# Revit family: Haworth_Tilt_Stool
name_source: partatom
category: Furniture
revit_build: Autodesk Revit 2018 (Build: 20170223_1515(x64)
units: mm (PartAtom-declared; Revit-internal decimal feet)

## family parameters
Always vertical = Yes
Cut with Voids When Loaded = No
OmniClass Number = 23.40.70.14.64.21
OmniClass Title = Systems Furniture
Room Calculation Point = No
Shared = No
Work Plane-Based = No

## types (1)
- Tilt
    Actual Seat Height = 28"
    Assembly Code = E2020200
    Base Finish = <By Category>
    Description = Haworth - Chair - Tilt
    Frame Finish = Haworth _ Metal _ Chrome
    Manufacturer = Haworth
    Model = Haworth - Chair - Tilt
    Revision Number = 3
    Seat Finish = Haworth _ Fabric _ Tellure _ Black 3A-18
    Seat Height = 28"
    Seat Height Max = 35"
    Seat Height Min = 26"
    Size = Verify Final Dim. w/ Haworth
    Standard Seat Heights = 26 in. - 35 in.
    Sustainability Info = http://www.haworth.com
    URL = http://haworth.com
    URL - Product = https://www.haworth.com
    Warranty = http://www.haworth.com

## geometry (parser evidence)
native form markers: Sweep x3
no freeform markers — native parametric forms only
